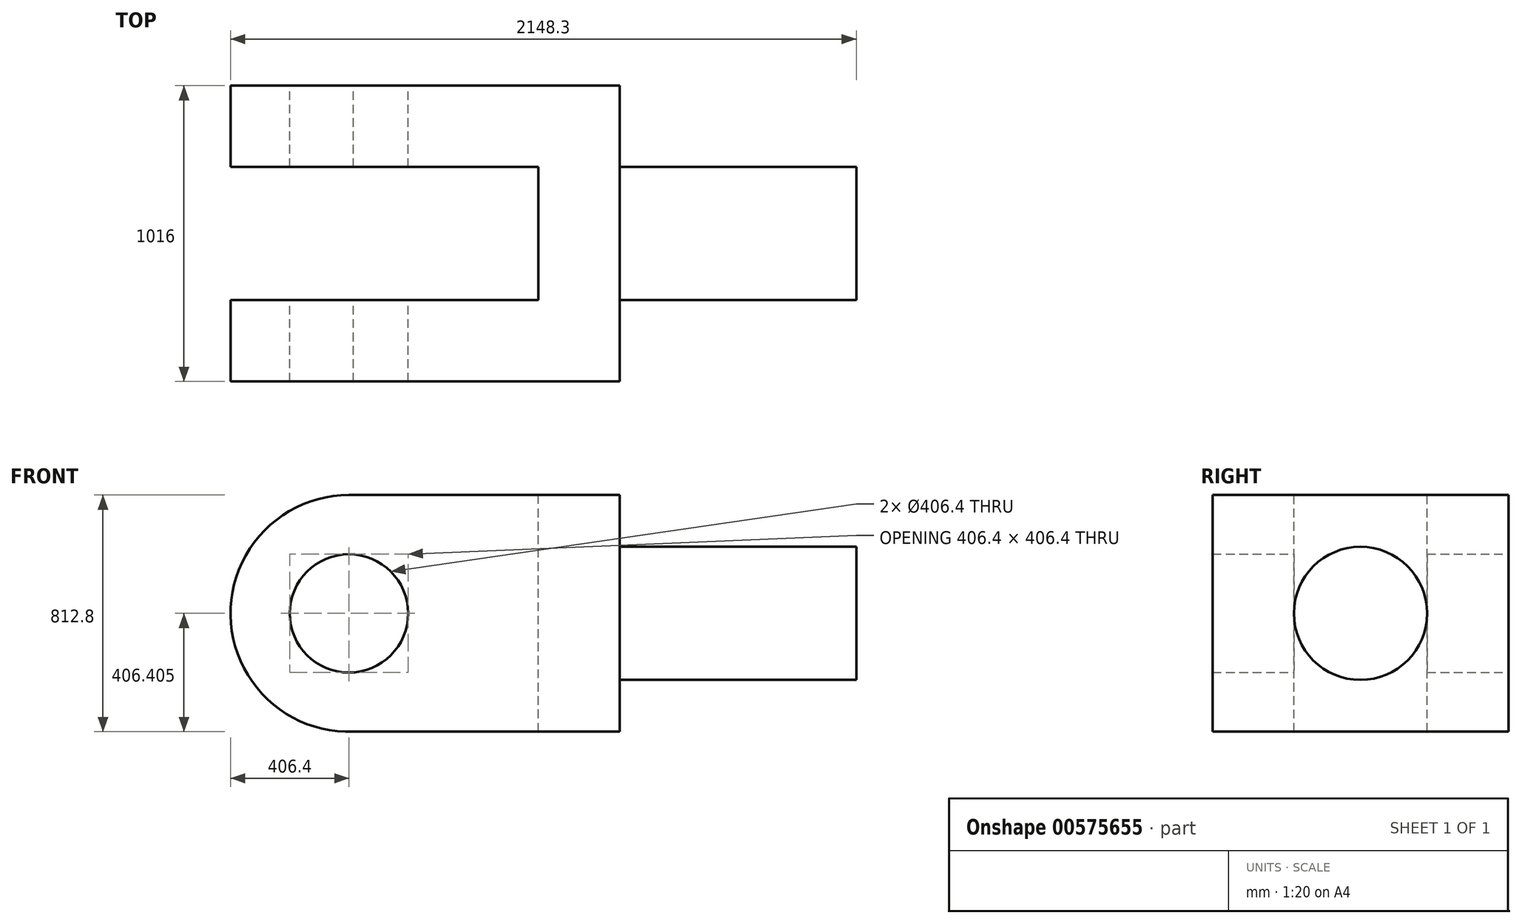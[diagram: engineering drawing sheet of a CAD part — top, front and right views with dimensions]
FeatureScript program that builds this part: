
annotation { "Feature Type Name" : "Feature", "Feature Type Description" : "" }
export const myFeature = defineFeature(function(context is Context, id is Id, definition is map)
    precondition{}
    {
        {
            var Q0;
            Q0=qCreatedBy(makeId("Front.planeOp"),FACE);
            var sketch = newSketch(context, id + "F0", { "sketchPlane" : qUnion([Q0])});
            skLineSegment(sketch, "E0", {"start": v(929.1, 56.26) * mm, "end": v(14.7, 56.26) * mm});
            skArc(sketch, "E1", {"start": v(0, 868.8) * mm, "mid": v(-406.33, 455.04) * mm, "end": v(14.7, 56.26) * mm});
            skCircle(sketch, "E2", {"center": v(0, 462.4) * mm, "radius": 203.2 * mm});
            skLineSegment(sketch, "E3", {"start": v(0, 868.8) * mm, "end": v(929.1, 868.8) * mm});
            skLineSegment(sketch, "E4", {"start": v(929.1, 56.26) * mm, "end": v(929.1, 868.8) * mm});
            skSolve(sketch);
        }
        {
            var Q0;
            Q0=makeQuery(id+"F0.imprint","IMPRINT",FACE,{"disambiguationData":[TD([[makeQuery(id+"F0.imprint","IMPRINT",EDGE,{"derivedFrom":sQuery(id+"F0.wireOp",EDGE,"E0")}),-1.0]])]});
            extrude(context, id + "F1", {"entities" : qUnion([Q0]), "depth" : 1016 * mm, "offsetDistance" : 25.4 * mm});
        }
        {
            var Q0;
            Q0=makeQuery(id+"F1.opExtrude","SWEPT_FACE",FACE,{"disambiguationData":[OSD([sQuery(id+"F0.wireOp",EDGE,"E4")])]});
            var sketch = newSketch(context, id + "F2", { "sketchPlane" : qUnion([Q0])});
            skCircle(sketch, "E5", {"center": v(-508, 462.4) * mm, "radius": 228.6 * mm});
            skSolve(sketch);
        }
        {
            var Q0;
            Q0=makeQuery(id+"F2.imprint","IMPRINT",FACE,{"disambiguationData":[TD([[makeQuery(id+"F2.imprint","IMPRINT",EDGE,{"derivedFrom":sQuery(id+"F2.wireOp",EDGE,"E5")}),1.0]])]});
            var Q1;
            Q1=sQuery(id+"F2.wireOp",EDGE,"E5");
            extrude(context, id + "F3", {"entities" : qUnion([Q0]), "operationType" : NewBodyOperationType.ADD, "surfaceEntities" : qUnion([Q1]), "depth" : 812.8 * mm, "offsetDistance" : 25.4 * mm});
        }
        {
            var Q0;
            Q0=makeQuery(id+"F1.opExtrude","SWEPT_FACE",FACE,{"disambiguationData":[OSD([sQuery(id+"F0.wireOp",EDGE,"E3")])]});
            var sketch = newSketch(context, id + "F4", { "sketchPlane" : qUnion([Q0])});
            skSolve(sketch);
        }
        {
            var Q0;
            {var subQ0=sQuery(id+"F0.wireOp",EDGE,"E3");Q0=makeQuery(id+"F4.imprint","IMPRINT",FACE,{"disambiguationData":[TD([[makeQuery(id+"F4.imprint","IMPRINT",EDGE,{"derivedFrom":makeQuery(id+"F1.opExtrude","CAP_EDGE",EDGE,{"disambiguationData":[OSD([subQ0])],"isStart":true})}),-1.0]])]});}
            var sketch = newSketch(context, id + "F5", { "sketchPlane" : qUnion([Q0])});
            skLineSegment(sketch, "E6", {"start": v(649.7, -279.4) * mm, "end": v(-533.12, -279.4) * mm});
            skLineSegment(sketch, "E7", {"start": v(649.7, -279.4) * mm, "end": v(649.7, -736.6) * mm});
            skLineSegment(sketch, "E8", {"start": v(649.7, -736.6) * mm, "end": v(-533.12, -736.6) * mm});
            skLineSegment(sketch, "E9", {"start": v(-533.12, -736.6) * mm, "end": v(-533.12, -279.4) * mm});
            skLineSegment(sketch, "E10", {"start": v(0, -279.4) * mm, "end": v(0, -736.6) * mm});
            skLineSegment(sketch, "E11", {"start": v(0, -736.6) * mm, "end": v(649.7, -736.6) * mm});
            skSolve(sketch);
        }
        {
            var Q0;
            {var subQ0=sQuery(id+"F5.wireOp",EDGE,"E9");Q0=makeQuery(id+"F5.imprint","IMPRINT",FACE,{"disambiguationData":[TD([[makeQuery(id+"F5.imprint","IMPRINT",EDGE,{"derivedFrom":subQ0}),-1.0]])]});}
            extrude(context, id + "F6", {"entities" : qUnion([Q0]), "operationType" : NewBodyOperationType.REMOVE, "endBound" : BoundingType.THROUGH_ALL, "oppositeDirection" : true, "depth" : 25.4 * mm, "offsetDistance" : 25.4 * mm});
        }
        {
            var Q0;
            Q0 = qSketchRegion(id + "F5", true);
            extrude(context, id + "F7", {"entities" : qUnion([Q0]), "operationType" : NewBodyOperationType.REMOVE, "endBound" : BoundingType.THROUGH_ALL, "oppositeDirection" : true, "depth" : 25.4 * mm, "offsetDistance" : 25.4 * mm});
        }
    });
